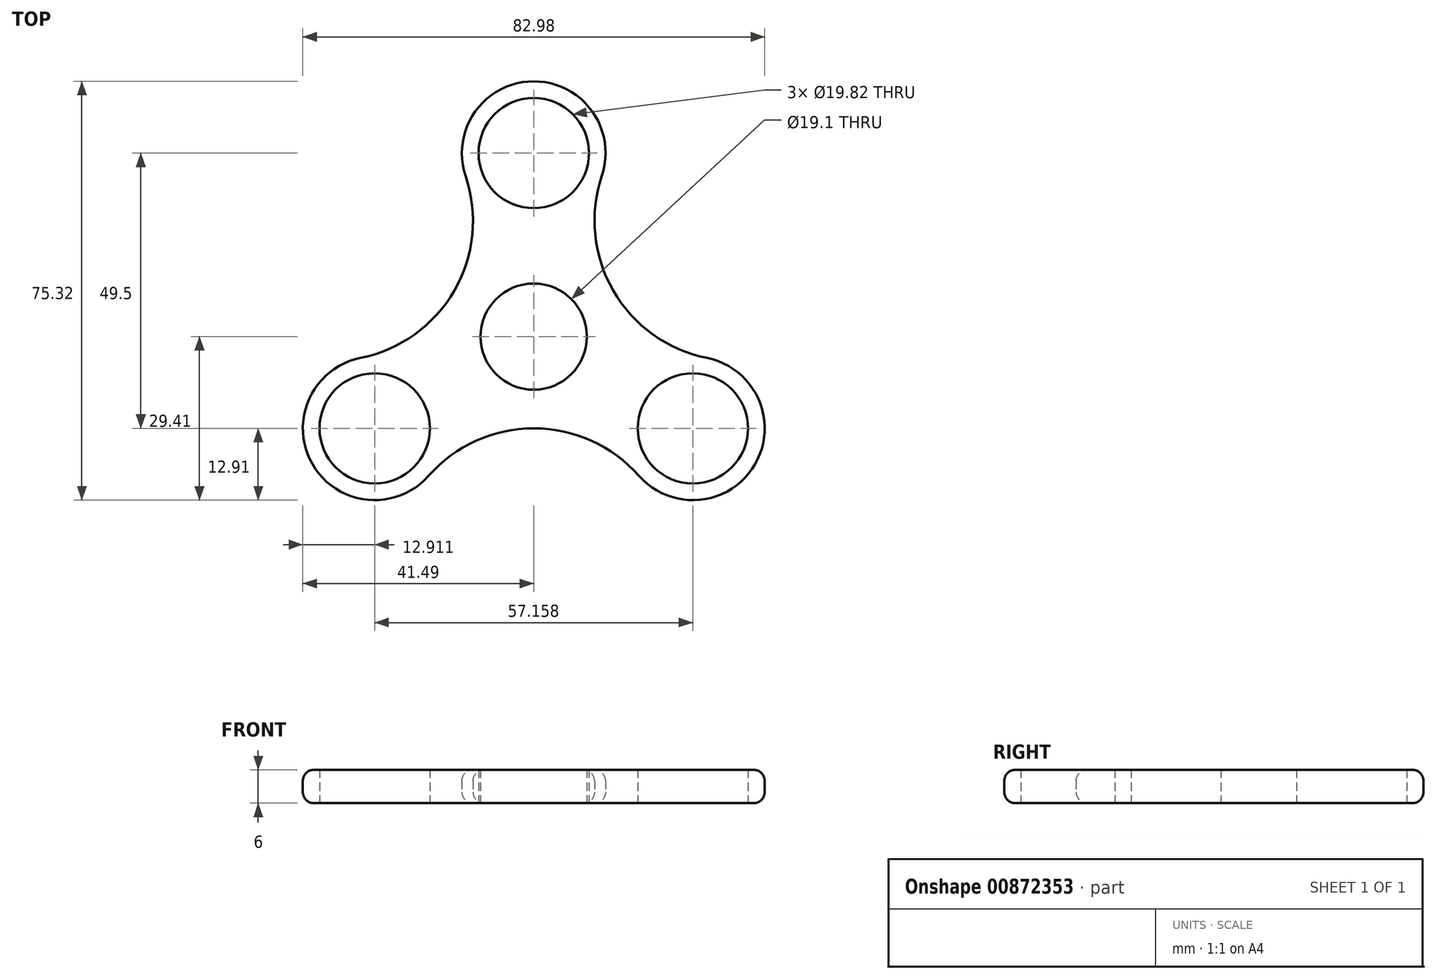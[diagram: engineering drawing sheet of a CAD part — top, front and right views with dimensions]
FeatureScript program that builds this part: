
annotation { "Feature Type Name" : "Feature", "Feature Type Description" : "" }
export const myFeature = defineFeature(function(context is Context, id is Id, definition is map)
    precondition{}
    {
        {
            var Q0;
            Q0=qCreatedBy(makeId("Top.planeOp"),FACE);
            var sketch = newSketch(context, id + "F0", { "sketchPlane" : qUnion([Q0])});
            skCircle(sketch, "E0", {"center": v(0, 0) * mm, "radius": 9.55 * mm});
            skCircle(sketch, "E1", {"center": v(0, 33) * mm, "radius": 9.9 * mm});
            skArc(sketch, "E2.0", {"start": v(12.23, 28.88) * mm, "mid": v(0, 45.9) * mm, "end": v(-12.23, 28.88) * mm});
            skCircle(sketch, "E3.1.0", {"center": v(-28.58, -16.5) * mm, "radius": 9.9 * mm});
            skArc(sketch, "E3.1.1", {"start": v(-31.13, -3.84) * mm, "mid": v(-39.76, -22.96) * mm, "end": v(-18.9, -25.03) * mm});
            skCircle(sketch, "E3.2.0", {"center": v(28.58, -16.5) * mm, "radius": 9.9 * mm});
            skArc(sketch, "E3.2.1", {"start": v(18.9, -25.03) * mm, "mid": v(39.76, -22.95) * mm, "end": v(31.13, -3.84) * mm});
            skLineSegment(sketch, "E4", {"start": v(-28.58, -16.5) * mm, "end": v(48.7, 28.12) * mm, "construction": true});
            skLineSegment(sketch, "E5", {"start": v(28.58, -16.5) * mm, "end": v(0, 33) * mm, "construction": true});
            skArc(sketch, "E6", {"start": v(12.23, 28.88) * mm, "mid": v(14.29, 8.25) * mm, "end": v(31.13, -3.84) * mm});
            skArc(sketch, "E7.1.0", {"start": v(-31.13, -3.84) * mm, "mid": v(-14.29, 8.25) * mm, "end": v(-12.23, 28.88) * mm});
            skArc(sketch, "E7.2.0", {"start": v(18.9, -25.03) * mm, "mid": v(0, -16.5) * mm, "end": v(-18.9, -25.03) * mm});
            skLineSegment(sketch, "E8", {"start": v(20, -11.54) * mm, "end": v(8.27, -4.77) * mm, "construction": true});
            skPoint(sketch, "E9", {"position": v(14.13, -8.16) * mm});
            skLineSegment(sketch, "E10", {"start": v(0, 0) * mm, "end": v(28.58, -16.5) * mm, "construction": true});
            skSolve(sketch);
        }
        {
            var Q0;
            Q0=makeQuery(id+"F0.imprint","IMPRINT",FACE,{"disambiguationData":[TD([[makeQuery(id+"F0.imprint","IMPRINT",EDGE,{"derivedFrom":sQuery(id+"F0.wireOp",EDGE,"E0")}),-1.0]])]});
            extrude(context, id + "F1", {"entities" : qUnion([Q0]), "depth" : 6 * mm, "offsetDistance" : 25 * mm});
        }
        {
            var Q0;
            Q0=makeQuery(id+"F1.opExtrude","CAP_EDGE",EDGE,{"disambiguationData":[OSD([sQuery(id+"F0.wireOp",EDGE,"E7.2.0")])],"isStart":false});
            var Q1;
            Q1=makeQuery(id+"F1.opExtrude","CAP_EDGE",EDGE,{"disambiguationData":[OSD([sQuery(id+"F0.wireOp",EDGE,"E7.2.0")])],"isStart":true});
            fillet(context, id + "F2", {"entities" : qUnion([Q0, Q1]), "radius" : 2 * mm, "tangentPropagation" : true, "allowEdgeOverflow" : false});
        }
    });
